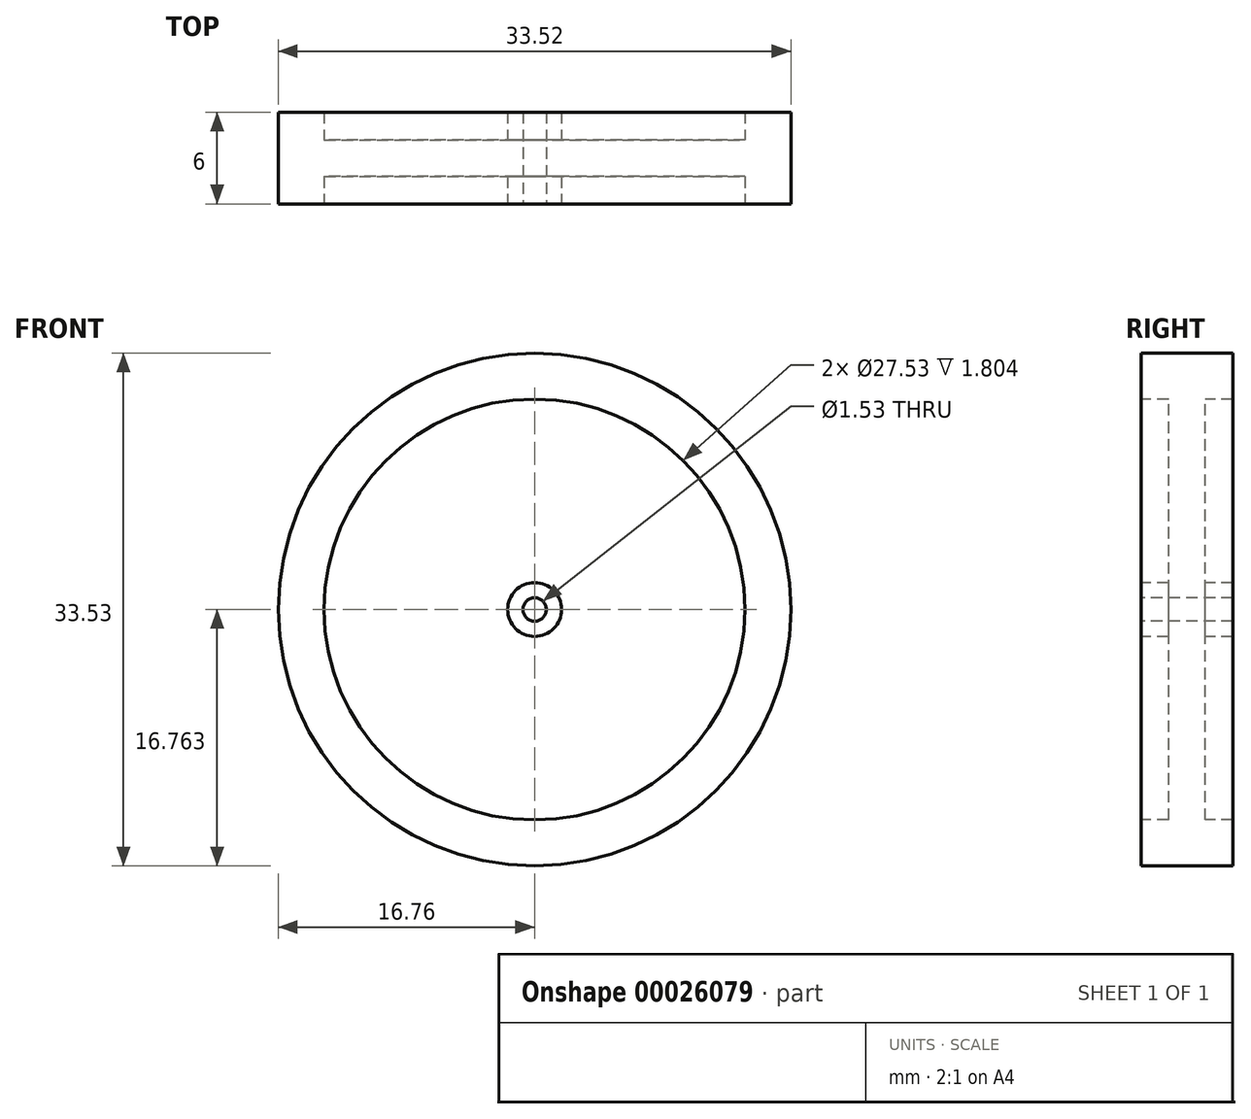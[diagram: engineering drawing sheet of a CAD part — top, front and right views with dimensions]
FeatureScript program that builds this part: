
annotation { "Feature Type Name" : "Feature", "Feature Type Description" : "" }
export const myFeature = defineFeature(function(context is Context, id is Id, definition is map)
    precondition{}
    {
        {
            var Q0;
            Q0=qCreatedBy(makeId("Right.planeOp"),FACE);
            var sketch = newSketch(context, id + "F0", { "sketchPlane" : qUnion([Q0])});
            skLineSegment(sketch, "E0", {"start": v(0, 0) * mm, "end": v(0, 3) * mm});
            skLineSegment(sketch, "E1", {"start": v(0, 3) * mm, "end": v(-1.8, 3) * mm});
            skLineSegment(sketch, "E2", {"start": v(-1.8, 3) * mm, "end": v(-1.8, 15) * mm});
            skLineSegment(sketch, "E3", {"start": v(-1.8, 15) * mm, "end": v(0, 15) * mm});
            skLineSegment(sketch, "E4", {"start": v(0, 15) * mm, "end": v(0, 16) * mm});
            skLineSegment(sketch, "E5", {"start": v(0, 16) * mm, "end": v(-6, 16) * mm});
            skLineSegment(sketch, "E6", {"start": v(-6, 16) * mm, "end": v(-6, 15) * mm});
            skLineSegment(sketch, "E7", {"start": v(-6, 15) * mm, "end": v(-4.2, 15) * mm});
            skLineSegment(sketch, "E8", {"start": v(-4.2, 15) * mm, "end": v(-4.2, 3) * mm});
            skLineSegment(sketch, "E9", {"start": v(-4.2, 3) * mm, "end": v(-6, 3) * mm});
            skLineSegment(sketch, "E10", {"start": v(-6, 3) * mm, "end": v(-6, 0) * mm});
            skLineSegment(sketch, "E11", {"start": v(-6, 0) * mm, "end": v(0, 0) * mm});
            skLineSegment(sketch, "E12", {"start": v(-7.66, 16.76) * mm, "end": v(2.25, 16.76) * mm, "construction": true});
            skSolve(sketch);
        }
        {
            var Q0;
            Q0 = qSketchRegion(id + "F0", true);
            var Q1;
            Q1=sQuery(id+"F0.wireOp",EDGE,"E12");
            revolve(context, id + "F1", {"entities" : qUnion([Q0]), "axis" : qUnion([Q1]), "revolveType" : RevolveType.FULL});
        }
    });
